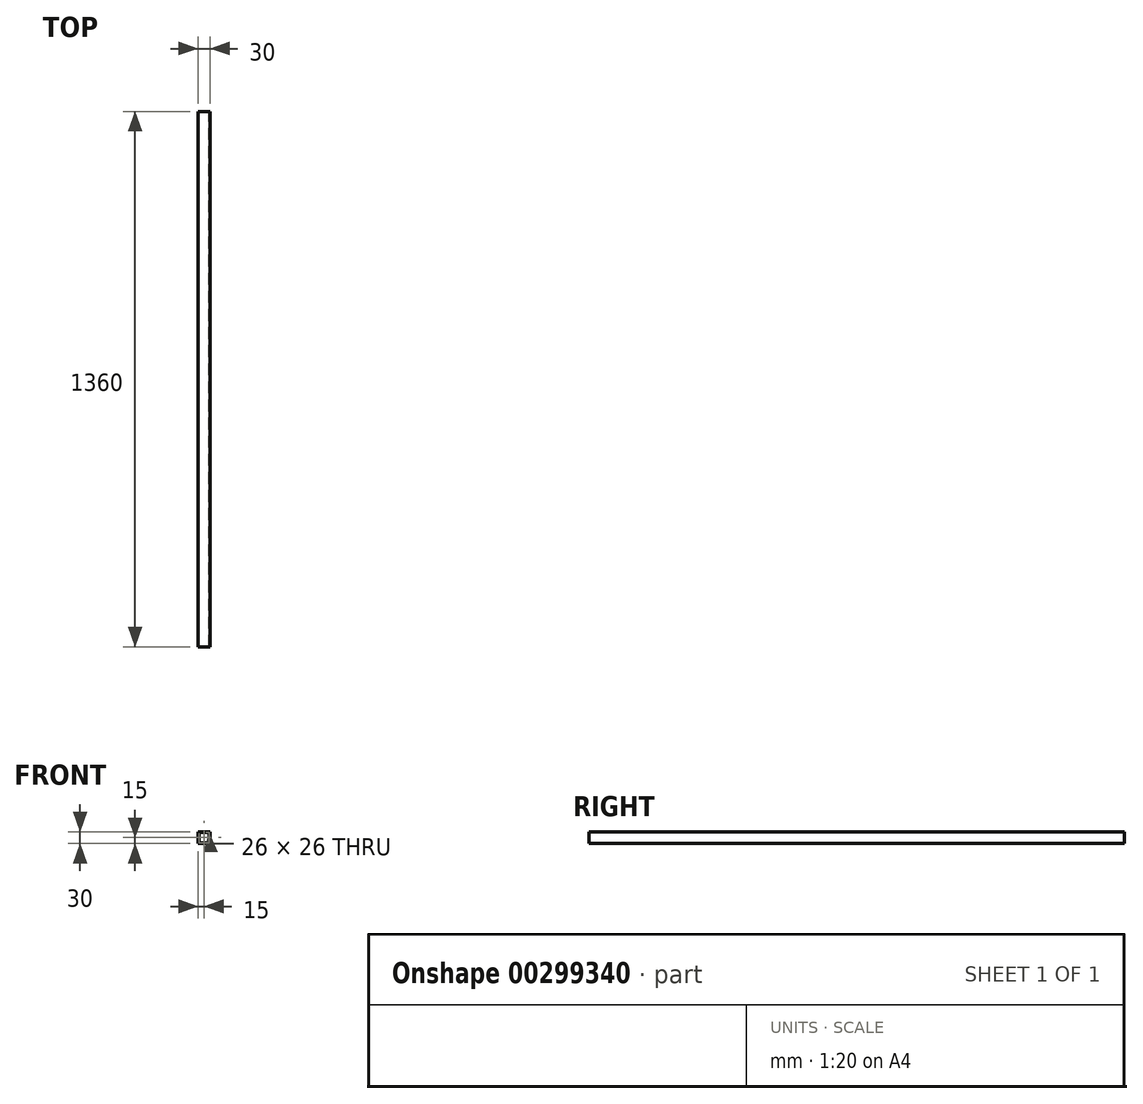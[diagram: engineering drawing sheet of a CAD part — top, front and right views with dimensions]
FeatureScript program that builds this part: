
annotation { "Feature Type Name" : "Feature", "Feature Type Description" : "" }
export const myFeature = defineFeature(function(context is Context, id is Id, definition is map)
    precondition{}
    {
        {
            var Q0;
            Q0=qCreatedBy(makeId("Front.planeOp"),FACE);
            var sketch = newSketch(context, id + "F0", { "sketchPlane" : qUnion([Q0])});
            skLineSegment(sketch, "E0.bottom", {"start": v(0, 0) * mm, "end": v(30, 0) * mm});
            skLineSegment(sketch, "E0.top", {"start": v(0, -30) * mm, "end": v(30, -30) * mm});
            skLineSegment(sketch, "E0.left", {"start": v(0, 0) * mm, "end": v(0, -30) * mm});
            skLineSegment(sketch, "E0.right", {"start": v(30, 0) * mm, "end": v(30, -30) * mm});
            skLineSegment(sketch, "E1.0", {"start": v(2, -2) * mm, "end": v(2, -28) * mm});
            skLineSegment(sketch, "E1.1", {"start": v(2, -2) * mm, "end": v(28, -2) * mm});
            skLineSegment(sketch, "E1.2", {"start": v(28, -2) * mm, "end": v(28, -28) * mm});
            skLineSegment(sketch, "E1.3", {"start": v(2, -28) * mm, "end": v(28, -28) * mm});
            skSolve(sketch);
        }
        {
            var Q0;
            Q0=makeQuery(id+"F0.imprint","IMPRINT",FACE,{"disambiguationData":[TD([[makeQuery(id+"F0.imprint","IMPRINT",EDGE,{"derivedFrom":sQuery(id+"F0.wireOp",EDGE,"E0.bottom")}),-1.0]])]});
            extrude(context, id + "F1", {"entities" : qUnion([Q0]), "depth" : 1360 * mm});
        }
    });
